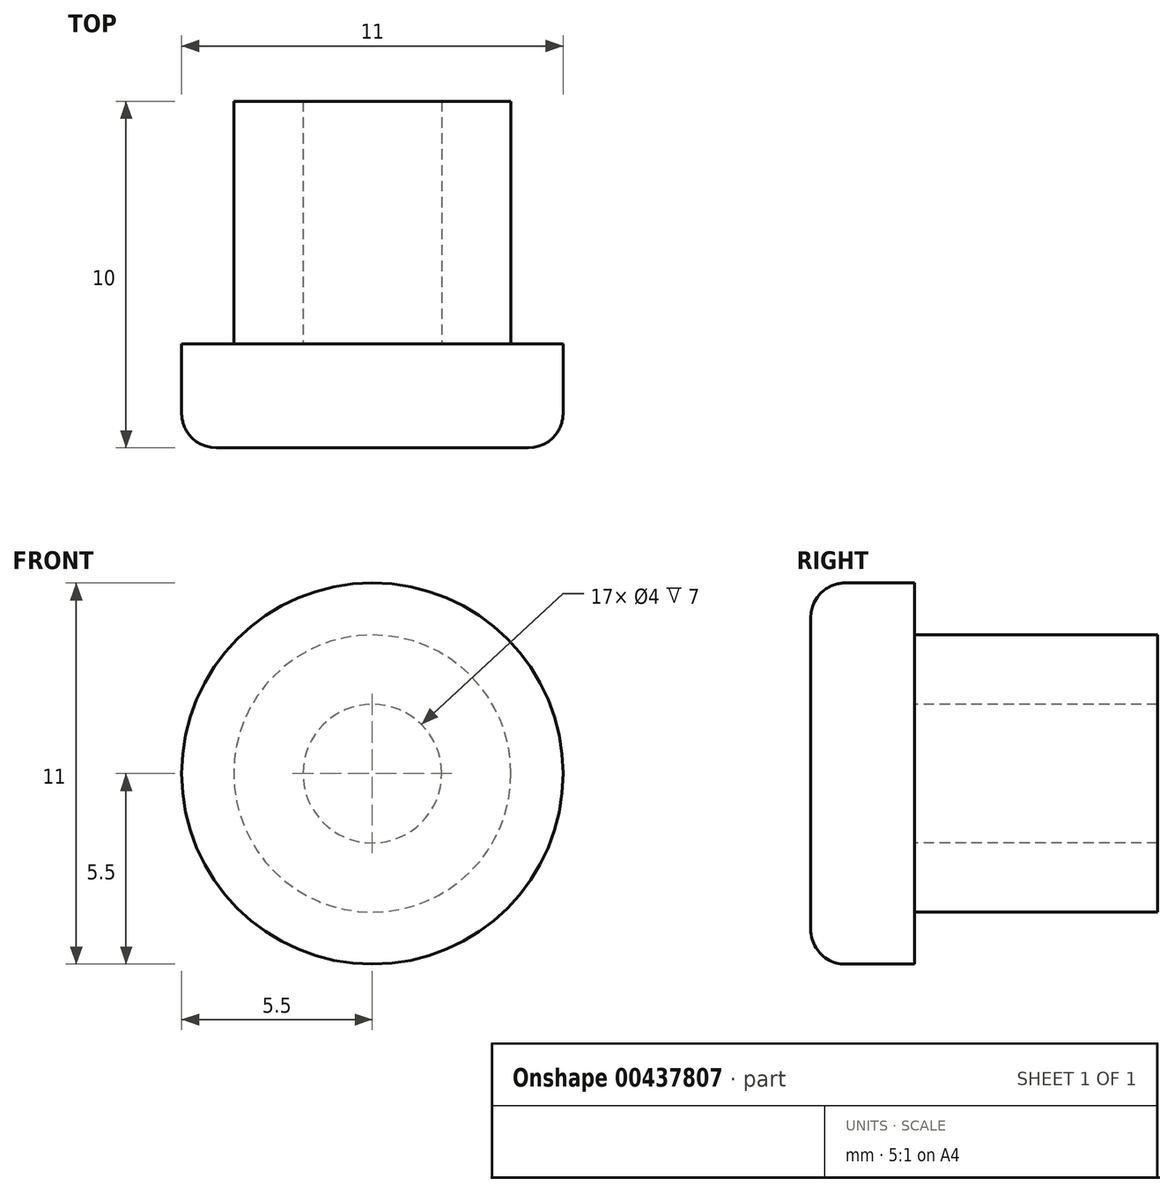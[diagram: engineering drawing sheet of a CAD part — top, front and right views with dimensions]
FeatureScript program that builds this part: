
annotation { "Feature Type Name" : "Feature", "Feature Type Description" : "" }
export const myFeature = defineFeature(function(context is Context, id is Id, definition is map)
    precondition{}
    {
        {
            var Q0;
            Q0=qCreatedBy(makeId("Top.planeOp"),FACE);
            var sketch = newSketch(context, id + "F0", { "sketchPlane" : qUnion([Q0])});
            skLineSegment(sketch, "E0", {"start": v(0, 0) * mm, "end": v(0, 12.5) * mm, "construction": true});
            skLineSegment(sketch, "E1", {"start": v(0, 0) * mm, "end": v(4.5, 0) * mm});
            skLineSegment(sketch, "E2", {"start": v(4, 3) * mm, "end": v(4, 10) * mm});
            skLineSegment(sketch, "E3", {"start": v(4, 10) * mm, "end": v(2, 10) * mm});
            skLineSegment(sketch, "E4", {"start": v(2, 10) * mm, "end": v(2, 3) * mm});
            skLineSegment(sketch, "E5", {"start": v(2, 3) * mm, "end": v(0, 3) * mm});
            skLineSegment(sketch, "E6", {"start": v(0, 3) * mm, "end": v(0, 0) * mm});
            skLineSegment(sketch, "E7", {"start": v(4, 3) * mm, "end": v(5.5, 3) * mm});
            skLineSegment(sketch, "E8", {"start": v(5.5, 3) * mm, "end": v(5.5, 1) * mm});
            skPoint(sketch, "E9.visualSharp", {"position": v(5.5, 0) * mm});
            skArc(sketch, "E9.filletArc", {"start": v(4.5, 0) * mm, "mid": v(5.2, 0.3) * mm, "end": v(5.5, 1) * mm});
            skLineSegment(sketch, "E10", {"start": v(2, 10) * mm, "end": v(0, 10) * mm});
            skLineSegment(sketch, "E11", {"start": v(0, 10) * mm, "end": v(0, 3) * mm});
            skLineSegment(sketch, "E12", {"start": v(2, 3) * mm, "end": v(4, 3) * mm});
            skSolve(sketch);
        }
        {
            var Q0;
            Q0=makeQuery(id+"F0.imprint","IMPRINT",FACE,{"disambiguationData":[TD([[makeQuery(id+"F0.imprint","IMPRINT",EDGE,{"derivedFrom":sQuery(id+"F0.wireOp",EDGE,"E1")}),1.0]])]});
            var Q1;
            Q1=makeQuery(id+"F0.imprint","IMPRINT",FACE,{"disambiguationData":[TD([[makeQuery(id+"F0.imprint","IMPRINT",EDGE,{"derivedFrom":sQuery(id+"F0.wireOp",EDGE,"E2")}),1.0]])]});
            var Q2;
            Q2=sQuery(id+"F0.wireOp",EDGE,"E0");
            revolve(context, id + "F1", {"surfaceOperationType" : NewSurfaceOperationType.NEW, "entities" : qUnion([Q0, Q1]), "axis" : qUnion([Q2]), "revolveType" : RevolveType.FULL});
        }
        {
            var Q0;
            Q0=makeQuery(id+"F0.imprint","IMPRINT",FACE,{"disambiguationData":[TD([[makeQuery(id+"F0.imprint","IMPRINT",EDGE,{"derivedFrom":sQuery(id+"F0.wireOp",EDGE,"E4")}),-1.0]])]});
            var Q1;
            Q1=makeQuery(id+"F0.imprint","IMPRINT",FACE,{"disambiguationData":[TD([[makeQuery(id+"F0.imprint","IMPRINT",EDGE,{"derivedFrom":sQuery(id+"F0.wireOp",EDGE,"E1")}),1.0]])]});
            var Q2;
            Q2=sQuery(id+"F0.wireOp",EDGE,"E0");
            revolve(context, id + "F2", {"surfaceOperationType" : NewSurfaceOperationType.NEW, "entities" : qUnion([Q0, Q1]), "axis" : qUnion([Q2]), "revolveType" : RevolveType.FULL});
        }
    });
